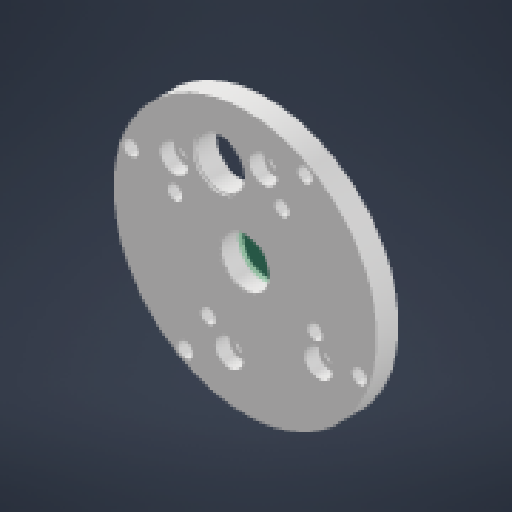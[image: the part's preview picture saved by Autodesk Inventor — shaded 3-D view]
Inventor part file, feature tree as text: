
AUTODESK INVENTOR PART (.ipt)
format: ipt  version: 2024.2 (Build 282272000, 272)  size: 220,672 bytes
history: native  units: in
note: dims shown in document units (in); Inventor stores cm internally (conversion verified against a paired STEP export)
features: reference x19, other x10, sketch x6, extrude x6, plane x2
ambient origin geometry x8: Origin, YZ Plane, XZ Plane, XY Plane, X Axis, Y Axis, Z Axis, Center Point
bodies: Solid1 (feature_tree)
feature tree (43):
  sketch  "Sketch1"  dims[d0=0.1693in d1=0.1693in]
  plane  "Work Plane1"
  extrude  "Extrusion1"  Depth=0.1693in
  plane  "Work Plane2"
  extrude  "Extrusion3"  Depth=0.1693in
  extrude  "Extrusion4"  Depth=0.0197in TaperAngle=0.0deg
  extrude  "Extrusion5"  Depth=0.5906in
  extrude  "Extrusion6"  Depth=0.002in
  extrude  "Extrusion7"  Depth=0.15in
  reference  "Reference1"
  reference  "Reference2"
  reference  "Reference3"
  reference  "Reference4"
  reference  "Reference5"
  reference  "Reference6"
  reference  "Reference7"
  sketch  "Sketch3"  dims[d2=0.1693in d3=0.1693in]
  reference  "Reference9"
  sketch  "Sketch5"  dims[d4=1.0in d5=0.0in d8=0.0197in d9=0.0in]
  reference  "Reference10"
  sketch  "Sketch6"  dims[d10=0.5906in d11=0.5906in]
  reference  "Reference11"
  reference  "Reference12"
  reference  "Reference13"
  reference  "Reference14"
  sketch  "Sketch7"  dims[d12=0.002in d13=0.0in d16=0.1693in]
  reference  "Reference15"
  reference  "Reference16"
  sketch  "Sketch8"  dims[d17=0.1693in d18=1.3944in d19=1.3944in d20=0.0in d21=0.1693in d22=0.1693in d23=0.0in d24=1.3944in d25=1.3944in d26=0.0in d27=0.002in d28=0.0in d29=0.315in d30=0.315in d31=0.15in d32=0.0in d33=0.1693in d34=0.1693in d35=0.0in d36=0.0in d37=0.315in d38=0.315in d39=0.0in d40=0.0in]
  reference  "Reference17"
  reference  "Reference18"
  reference  "Reference19"
  reference  "Reference20"
  other  "<userpath>\Desktop\Robotics\Swerve2\Assemblies\Pod.iam"
  other  "Pod.iam"
  other  "3ID3.5OD_Bearing:1"
  parser-record x1  (decoder bookkeeping rows leaked as tree rows — omitted from the tree; the rows remain in map.json)
  other  "1501 Series M4 x 0.7mm Standoff (6mm OD, 8mm Length) - 4 Pack:4"
  other  "1501 Series M4 x 0.7mm Standoff (6mm OD, 8mm Length) - 4 Pack:3"
  other  "1501 Series M4 x 0.7mm Standoff (6mm OD, 8mm Length) - 4 Pack:2"
  other  "1501 Series M4 x 0.7mm Standoff (6mm OD, 8mm Length) - 4 Pack:1"
  other  "Wheel_Axle_Holder:1"
  other  "Wheel_Axle_Holder_MIR:1"
